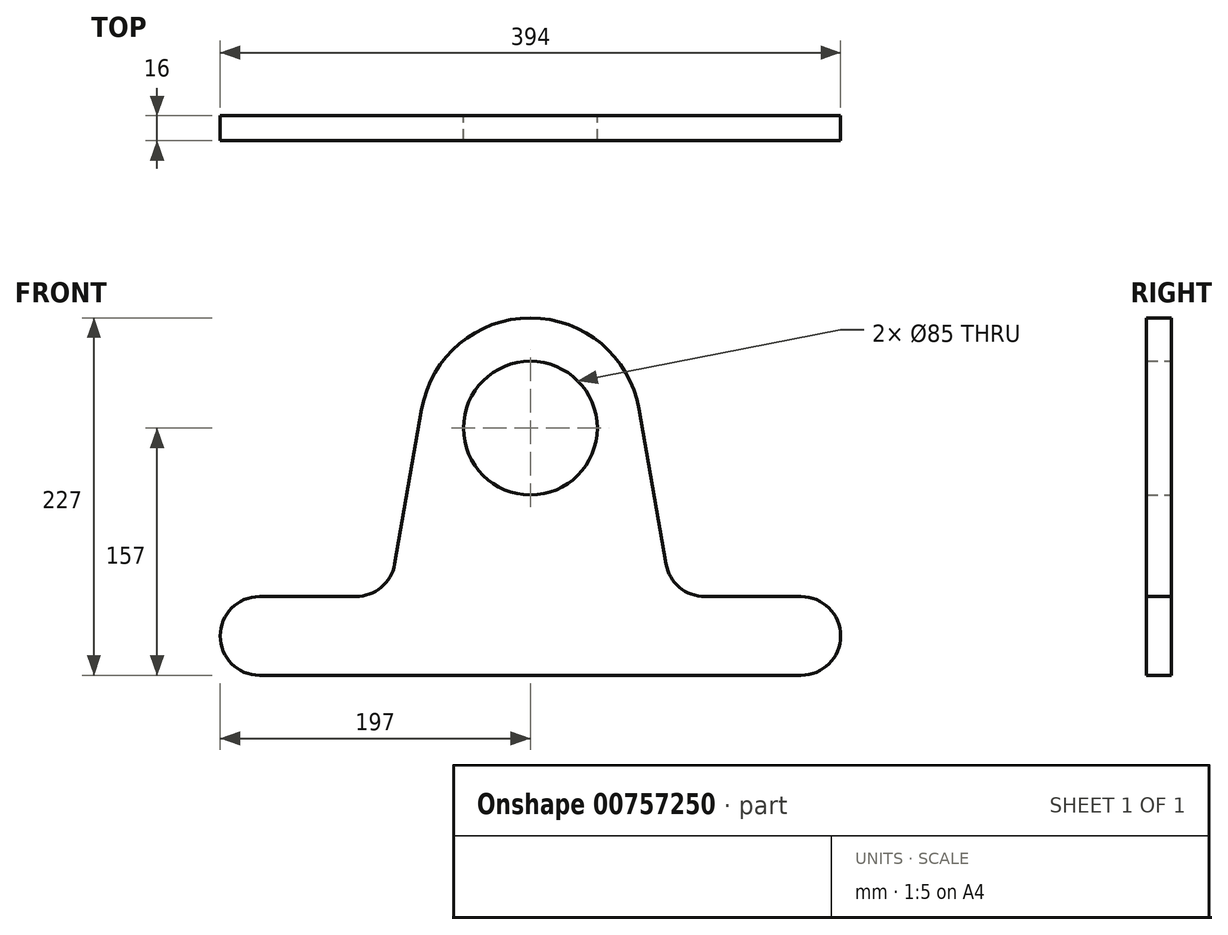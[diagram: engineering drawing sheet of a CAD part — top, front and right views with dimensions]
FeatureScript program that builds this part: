
annotation { "Feature Type Name" : "Feature", "Feature Type Description" : "" }
export const myFeature = defineFeature(function(context is Context, id is Id, definition is map)
    precondition{}
    {
        {
            var Q0;
            Q0=qCreatedBy(makeId("Front.planeOp"),FACE);
            var sketch = newSketch(context, id + "F0", { "sketchPlane" : qUnion([Q0])});
            skLineSegment(sketch, "E0", {"start": v(-172, 0) * mm, "end": v(172, 0) * mm});
            skLineSegment(sketch, "E1", {"start": v(-201.43, 25) * mm, "end": v(204.97, 25) * mm, "construction": true});
            skLineSegment(sketch, "E2", {"start": v(0, -15.45) * mm, "end": v(0, 225.78) * mm, "construction": true});
            skLineSegment(sketch, "E3", {"start": v(-172, 50) * mm, "end": v(-110.8, 50) * mm});
            skLineSegment(sketch, "E4", {"start": v(-144.58, 157) * mm, "end": v(136.6, 157) * mm, "construction": true});
            skCircle(sketch, "E5", {"center": v(0, 157) * mm, "radius": 42.5 * mm});
            skArc(sketch, "E6", {"start": v(68.95, 169.07) * mm, "mid": v(0, 227) * mm, "end": v(-68.95, 169.07) * mm});
            skPoint(sketch, "E7", {"position": v(-89.8, 50) * mm});
            skLineSegment(sketch, "E8", {"start": v(-86.18, 70.69) * mm, "end": v(-68.95, 169.07) * mm});
            skLineSegment(sketch, "E9.MirrorCS", {"start": v(86.18, 70.69) * mm, "end": v(68.95, 169.07) * mm});
            skPoint(sketch, "E10.third.point", {"position": v(-197, 0) * mm});
            skLineSegment(sketch, "E11.trimOffspring", {"start": v(110.8, 50) * mm, "end": v(172, 50) * mm});
            skArc(sketch, "E12.filletArc", {"start": v(-110.8, 50) * mm, "mid": v(-94.72, 55.86) * mm, "end": v(-86.18, 70.69) * mm});
            skPoint(sketch, "E13.visualSharp", {"position": v(89.8, 50) * mm});
            skArc(sketch, "E13.filletArc", {"start": v(86.18, 70.69) * mm, "mid": v(94.72, 55.86) * mm, "end": v(110.8, 50) * mm});
            skArc(sketch, "E14", {"start": v(-172, 50) * mm, "mid": v(-197, 25) * mm, "end": v(-172, 0) * mm});
            skArc(sketch, "E15.MirrorCS", {"start": v(172, 50) * mm, "mid": v(197, 25) * mm, "end": v(172, 0) * mm});
            skSolve(sketch);
        }
        {
            var Q0;
            Q0 = qSketchRegion(id + "F0", true);
            extrude(context, id + "F1", {"entities" : qUnion([Q0]), "depth" : 16 * mm, "offsetDistance" : 25 * mm});
        }
    });
